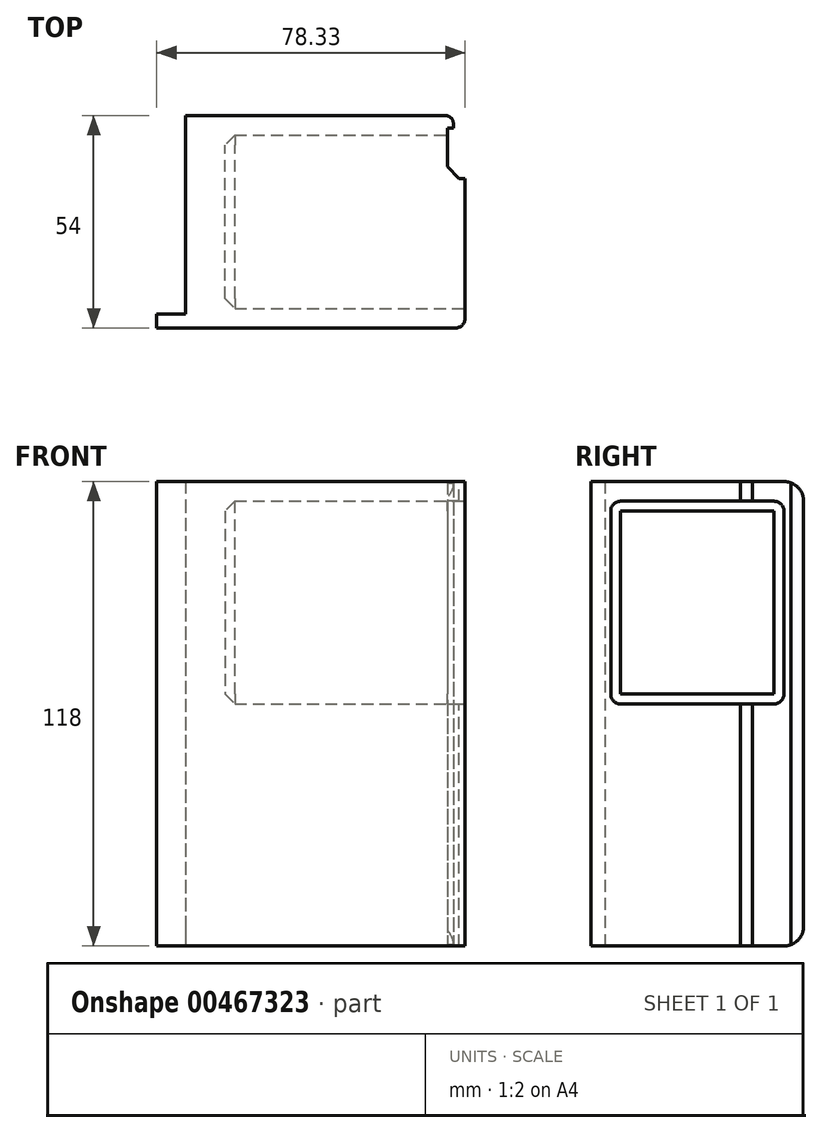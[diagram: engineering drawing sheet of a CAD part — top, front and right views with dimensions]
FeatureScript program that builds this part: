
annotation { "Feature Type Name" : "Feature", "Feature Type Description" : "" }
export const myFeature = defineFeature(function(context is Context, id is Id, definition is map)
    precondition{}
    {
        {
            var Q0;
            Q0=qCreatedBy(makeId("Top.planeOp"),FACE);
            var sketch = newSketch(context, id + "F0", { "sketchPlane" : qUnion([Q0])});
            skLineSegment(sketch, "E0", {"start": v(15.39, 4.66) * mm, "end": v(15.39, 8.16) * mm});
            skLineSegment(sketch, "E1", {"start": v(15.39, 8.16) * mm, "end": v(22.72, 8.16) * mm});
            skLineSegment(sketch, "E2", {"start": v(22.72, 8.16) * mm, "end": v(22.72, 58.66) * mm});
            skLineSegment(sketch, "E3", {"start": v(22.72, 58.66) * mm, "end": v(93.72, 58.66) * mm});
            skLineSegment(sketch, "E4", {"start": v(93.72, 58.66) * mm, "end": v(93.72, 4.66) * mm});
            skLineSegment(sketch, "E5", {"start": v(93.72, 4.66) * mm, "end": v(15.39, 4.66) * mm});
            skLineSegment(sketch, "E6", {"start": v(90.72, 58.66) * mm, "end": v(90.72, 55.46) * mm});
            skLineSegment(sketch, "E7", {"start": v(90.72, 55.46) * mm, "end": v(89.22, 55.46) * mm});
            skLineSegment(sketch, "E8", {"start": v(89.22, 55.46) * mm, "end": v(89.22, 42.66) * mm});
            skLineSegment(sketch, "E9", {"start": v(89.22, 42.66) * mm, "end": v(93.72, 42.66) * mm});
            skSolve(sketch);
        }
        {
            var Q0;
            Q0=makeQuery(id+"F0.imprint","IMPRINT",FACE,{"disambiguationData":[TD([[makeQuery(id+"F0.imprint","IMPRINT",EDGE,{"derivedFrom":sQuery(id+"F0.wireOp",EDGE,"E0")}),-1.0]])]});
            extrude(context, id + "F1", {"entities" : qUnion([Q0]), "depth" : 118 * mm});
        }
        {
            var Q0;
            Q0=makeQuery(id+"F1.opExtrude","SWEPT_FACE",FACE,{"disambiguationData":[OSD([sQuery(id+"F0.wireOp",EDGE,"E4")])]});
            var sketch = newSketch(context, id + "F2", { "sketchPlane" : qUnion([Q0])});
            skLineSegment(sketch, "E10", {"start": v(23.66, 119.82) * mm, "end": v(23.66, 0) * mm, "construction": true});
            skPoint(sketch, "E10.startSnap0", {"position": v(23.66, 118) * mm});
            skLineSegment(sketch, "E11", {"start": v(58.66, 59) * mm, "end": v(4.66, 59) * mm, "construction": true});
            skLineSegment(sketch, "E12", {"start": v(58.66, 78.67) * mm, "end": v(4.66, 78.67) * mm, "construction": true});
            skLineSegment(sketch, "E13.MirrorCS", {"start": v(58.66, 39.33) * mm, "end": v(4.66, 39.33) * mm, "construction": true});
            skLineSegment(sketch, "E14.0", {"start": v(42.66, 118) * mm, "end": v(42.66, 0) * mm});
            skLineSegment(sketch, "E15.0.0", {"start": v(4.66, 0) * mm, "end": v(42.66, 0) * mm});
            skLineSegment(sketch, "E15.0.1", {"start": v(42.66, 0) * mm, "end": v(42.66, 118) * mm});
            skLineSegment(sketch, "E15.0.2", {"start": v(42.66, 118) * mm, "end": v(4.66, 118) * mm});
            skLineSegment(sketch, "E15.0.3", {"start": v(4.66, 118) * mm, "end": v(4.66, 0) * mm});
            skLineSegment(sketch, "E16.bottom", {"start": v(35.16, 113) * mm, "end": v(28.66, 113) * mm});
            skLineSegment(sketch, "E16.top", {"start": v(35.16, 81.17) * mm, "end": v(28.66, 81.17) * mm});
            skLineSegment(sketch, "E16.left", {"start": v(37.66, 110.5) * mm, "end": v(37.66, 83.67) * mm});
            skLineSegment(sketch, "E16.right", {"start": v(26.16, 110.5) * mm, "end": v(26.16, 83.67) * mm});
            skLineSegment(sketch, "E17.MirrorCS", {"start": v(12.16, 113) * mm, "end": v(18.66, 113) * mm});
            skLineSegment(sketch, "E18.MirrorCS", {"start": v(21.16, 110.5) * mm, "end": v(21.16, 83.67) * mm});
            skLineSegment(sketch, "E19.MirrorCS", {"start": v(9.66, 110.5) * mm, "end": v(9.66, 83.67) * mm});
            skLineSegment(sketch, "E20.MirrorCS", {"start": v(12.16, 81.17) * mm, "end": v(18.66, 81.17) * mm});
            skLineSegment(sketch, "E21.MirrorCS", {"start": v(35.16, 76.17) * mm, "end": v(28.66, 76.17) * mm});
            skLineSegment(sketch, "E22.MirrorCS", {"start": v(12.16, 76.17) * mm, "end": v(18.66, 76.17) * mm});
            skLineSegment(sketch, "E23", {"start": v(37.66, 73.67) * mm, "end": v(37.66, 44.33) * mm});
            skLineSegment(sketch, "E24", {"start": v(35.16, 41.83) * mm, "end": v(28.66, 41.83) * mm});
            skLineSegment(sketch, "E25", {"start": v(26.16, 44.33) * mm, "end": v(26.16, 73.67) * mm});
            skLineSegment(sketch, "E26.MirrorCS", {"start": v(21.16, 44.33) * mm, "end": v(21.16, 73.67) * mm});
            skLineSegment(sketch, "E27.MirrorCS", {"start": v(12.16, 41.83) * mm, "end": v(18.66, 41.83) * mm});
            skLineSegment(sketch, "E28.MirrorCS", {"start": v(9.66, 73.67) * mm, "end": v(9.66, 44.33) * mm});
            skLineSegment(sketch, "E29.MirrorCS", {"start": v(35.16, 36.83) * mm, "end": v(28.66, 36.83) * mm});
            skLineSegment(sketch, "E30.MirrorCS", {"start": v(12.16, 36.83) * mm, "end": v(18.66, 36.83) * mm});
            skLineSegment(sketch, "E31", {"start": v(37.66, 34.33) * mm, "end": v(37.66, 7.5) * mm});
            skLineSegment(sketch, "E32", {"start": v(35.16, 5) * mm, "end": v(28.66, 5) * mm});
            skLineSegment(sketch, "E33", {"start": v(26.16, 7.5) * mm, "end": v(26.16, 34.33) * mm});
            skLineSegment(sketch, "E34.MirrorCS", {"start": v(21.16, 7.5) * mm, "end": v(21.16, 34.33) * mm});
            skLineSegment(sketch, "E35.MirrorCS", {"start": v(12.16, 5) * mm, "end": v(18.66, 5) * mm});
            skLineSegment(sketch, "E36.MirrorCS", {"start": v(9.66, 34.33) * mm, "end": v(9.66, 7.5) * mm});
            skPoint(sketch, "E37.visualSharp", {"position": v(37.66, 113) * mm});
            skArc(sketch, "E37.filletArc", {"start": v(37.66, 110.5) * mm, "mid": v(36.92, 112.27) * mm, "end": v(35.16, 113) * mm});
            skPoint(sketch, "E38.visualSharp", {"position": v(26.16, 113) * mm});
            skArc(sketch, "E38.filletArc", {"start": v(28.66, 113) * mm, "mid": v(26.89, 112.27) * mm, "end": v(26.16, 110.5) * mm});
            skPoint(sketch, "E39.visualSharp", {"position": v(26.16, 81.17) * mm});
            skArc(sketch, "E39.filletArc", {"start": v(26.16, 83.67) * mm, "mid": v(26.89, 81.9) * mm, "end": v(28.66, 81.17) * mm});
            skPoint(sketch, "E40.visualSharp", {"position": v(37.66, 81.17) * mm});
            skArc(sketch, "E40.filletArc", {"start": v(35.16, 81.17) * mm, "mid": v(36.92, 81.9) * mm, "end": v(37.66, 83.67) * mm});
            skPoint(sketch, "E41.visualSharp", {"position": v(37.66, 76.17) * mm});
            skArc(sketch, "E41.filletArc", {"start": v(37.66, 73.67) * mm, "mid": v(36.92, 75.43) * mm, "end": v(35.16, 76.17) * mm});
            skPoint(sketch, "E42.visualSharp", {"position": v(26.16, 76.17) * mm});
            skArc(sketch, "E42.filletArc", {"start": v(28.66, 76.17) * mm, "mid": v(26.89, 75.43) * mm, "end": v(26.16, 73.67) * mm});
            skPoint(sketch, "E43.visualSharp", {"position": v(26.16, 41.83) * mm});
            skArc(sketch, "E43.filletArc", {"start": v(26.16, 44.33) * mm, "mid": v(26.89, 42.57) * mm, "end": v(28.66, 41.83) * mm});
            skPoint(sketch, "E44.visualSharp", {"position": v(37.66, 41.83) * mm});
            skArc(sketch, "E44.filletArc", {"start": v(35.16, 41.83) * mm, "mid": v(36.92, 42.57) * mm, "end": v(37.66, 44.33) * mm});
            skPoint(sketch, "E45.visualSharp", {"position": v(37.66, 36.83) * mm});
            skArc(sketch, "E45.filletArc", {"start": v(37.66, 34.33) * mm, "mid": v(36.92, 36.1) * mm, "end": v(35.16, 36.83) * mm});
            skPoint(sketch, "E46.visualSharp", {"position": v(26.16, 36.83) * mm});
            skArc(sketch, "E46.filletArc", {"start": v(28.66, 36.83) * mm, "mid": v(26.89, 36.1) * mm, "end": v(26.16, 34.33) * mm});
            skPoint(sketch, "E47.visualSharp", {"position": v(26.16, 5) * mm});
            skArc(sketch, "E47.filletArc", {"start": v(26.16, 7.5) * mm, "mid": v(26.89, 5.73) * mm, "end": v(28.66, 5) * mm});
            skPoint(sketch, "E48.visualSharp", {"position": v(37.66, 5) * mm});
            skArc(sketch, "E48.filletArc", {"start": v(35.16, 5) * mm, "mid": v(36.92, 5.73) * mm, "end": v(37.66, 7.5) * mm});
            skPoint(sketch, "E49.visualSharp", {"position": v(21.16, 113) * mm});
            skArc(sketch, "E49.filletArc", {"start": v(21.16, 110.5) * mm, "mid": v(20.42, 112.27) * mm, "end": v(18.66, 113) * mm});
            skPoint(sketch, "E50.visualSharp", {"position": v(9.66, 113) * mm});
            skArc(sketch, "E50.filletArc", {"start": v(12.16, 113) * mm, "mid": v(10.39, 112.27) * mm, "end": v(9.66, 110.5) * mm});
            skPoint(sketch, "E51.visualSharp", {"position": v(9.66, 81.17) * mm});
            skArc(sketch, "E51.filletArc", {"start": v(9.66, 83.67) * mm, "mid": v(10.39, 81.9) * mm, "end": v(12.16, 81.17) * mm});
            skPoint(sketch, "E52.visualSharp", {"position": v(21.16, 81.17) * mm});
            skArc(sketch, "E52.filletArc", {"start": v(18.66, 81.17) * mm, "mid": v(20.42, 81.9) * mm, "end": v(21.16, 83.67) * mm});
            skPoint(sketch, "E53.visualSharp", {"position": v(21.16, 76.17) * mm});
            skArc(sketch, "E53.filletArc", {"start": v(21.16, 73.67) * mm, "mid": v(20.42, 75.43) * mm, "end": v(18.66, 76.17) * mm});
            skPoint(sketch, "E54.visualSharp", {"position": v(9.66, 76.17) * mm});
            skArc(sketch, "E54.filletArc", {"start": v(12.16, 76.17) * mm, "mid": v(10.39, 75.43) * mm, "end": v(9.66, 73.67) * mm});
            skPoint(sketch, "E55.visualSharp", {"position": v(21.16, 41.83) * mm});
            skArc(sketch, "E55.filletArc", {"start": v(18.66, 41.83) * mm, "mid": v(20.42, 42.57) * mm, "end": v(21.16, 44.33) * mm});
            skPoint(sketch, "E56.visualSharp", {"position": v(9.66, 41.83) * mm});
            skArc(sketch, "E56.filletArc", {"start": v(9.66, 44.33) * mm, "mid": v(10.39, 42.57) * mm, "end": v(12.16, 41.83) * mm});
            skPoint(sketch, "E57.visualSharp", {"position": v(9.66, 36.83) * mm});
            skArc(sketch, "E57.filletArc", {"start": v(12.16, 36.83) * mm, "mid": v(10.39, 36.1) * mm, "end": v(9.66, 34.33) * mm});
            skPoint(sketch, "E58.visualSharp", {"position": v(21.16, 36.83) * mm});
            skArc(sketch, "E58.filletArc", {"start": v(21.16, 34.33) * mm, "mid": v(20.42, 36.1) * mm, "end": v(18.66, 36.83) * mm});
            skPoint(sketch, "E59.visualSharp", {"position": v(21.16, 5) * mm});
            skArc(sketch, "E59.filletArc", {"start": v(18.66, 5) * mm, "mid": v(20.42, 5.73) * mm, "end": v(21.16, 7.5) * mm});
            skPoint(sketch, "E60.visualSharp", {"position": v(9.66, 5) * mm});
            skArc(sketch, "E60.filletArc", {"start": v(9.66, 7.5) * mm, "mid": v(10.39, 5.73) * mm, "end": v(12.16, 5) * mm});
            skSolve(sketch);
        }
        {
            var Q0;
            Q0=makeQuery(id+"F1.opExtrude","SWEPT_FACE",FACE,{"disambiguationData":[OSD([sQuery(id+"F0.wireOp",EDGE,"E4")])]});
            var sketch = newSketch(context, id + "F3", { "sketchPlane" : qUnion([Q0])});
            skLineSegment(sketch, "E61.0", {"start": v(58.66, 118) * mm, "end": v(58.66, 0) * mm});
            skLineSegment(sketch, "E62.0", {"start": v(4.66, 118) * mm, "end": v(4.66, 0) * mm});
            skLineSegment(sketch, "E63.0", {"start": v(42.66, 118) * mm, "end": v(4.66, 118) * mm});
            skLineSegment(sketch, "E64.0", {"start": v(42.66, 0) * mm, "end": v(4.66, 0) * mm});
            skLineSegment(sketch, "E65.0", {"start": v(55.46, 0) * mm, "end": v(42.66, 0) * mm});
            skLineSegment(sketch, "E66.0", {"start": v(58.66, 0) * mm, "end": v(55.46, 0) * mm});
            skLineSegment(sketch, "E67.0", {"start": v(58.66, 118) * mm, "end": v(55.46, 118) * mm});
            skLineSegment(sketch, "E68.0", {"start": v(55.46, 118) * mm, "end": v(42.66, 118) * mm});
            skLineSegment(sketch, "E69", {"start": v(58.66, 59) * mm, "end": v(4.66, 59) * mm, "construction": true});
            skLineSegment(sketch, "E70.bottom", {"start": v(51.16, 113) * mm, "end": v(12.16, 113) * mm});
            skLineSegment(sketch, "E70.top", {"start": v(51.16, 61.5) * mm, "end": v(12.16, 61.5) * mm});
            skLineSegment(sketch, "E70.left", {"start": v(53.66, 110.5) * mm, "end": v(53.66, 64) * mm});
            skLineSegment(sketch, "E70.right", {"start": v(9.66, 110.5) * mm, "end": v(9.66, 64) * mm});
            skPoint(sketch, "E71.visualSharp", {"position": v(53.66, 113) * mm});
            skArc(sketch, "E71.filletArc", {"start": v(53.66, 110.5) * mm, "mid": v(52.92, 112.27) * mm, "end": v(51.16, 113) * mm});
            skPoint(sketch, "E72.visualSharp", {"position": v(9.66, 113) * mm});
            skArc(sketch, "E72.filletArc", {"start": v(12.16, 113) * mm, "mid": v(10.39, 112.27) * mm, "end": v(9.66, 110.5) * mm});
            skPoint(sketch, "E73.visualSharp", {"position": v(9.66, 61.5) * mm});
            skArc(sketch, "E73.filletArc", {"start": v(9.66, 64) * mm, "mid": v(10.39, 62.23) * mm, "end": v(12.16, 61.5) * mm});
            skPoint(sketch, "E74.visualSharp", {"position": v(53.66, 61.5) * mm});
            skArc(sketch, "E74.filletArc", {"start": v(51.16, 61.5) * mm, "mid": v(52.92, 62.23) * mm, "end": v(53.66, 64) * mm});
            skLineSegment(sketch, "E75.MirrorCS", {"start": v(51.16, 56.5) * mm, "end": v(12.16, 56.5) * mm});
            skArc(sketch, "E76.MirrorCS", {"start": v(9.66, 54) * mm, "mid": v(10.39, 55.77) * mm, "end": v(12.16, 56.5) * mm});
            skLineSegment(sketch, "E77.MirrorCS", {"start": v(9.66, 7.5) * mm, "end": v(9.66, 54) * mm});
            skArc(sketch, "E78.MirrorCS", {"start": v(12.16, 5) * mm, "mid": v(10.39, 5.73) * mm, "end": v(9.66, 7.5) * mm});
            skLineSegment(sketch, "E79.MirrorCS", {"start": v(51.16, 5) * mm, "end": v(12.16, 5) * mm});
            skArc(sketch, "E80.MirrorCS", {"start": v(53.66, 7.5) * mm, "mid": v(52.92, 5.73) * mm, "end": v(51.16, 5) * mm});
            skLineSegment(sketch, "E81.MirrorCS", {"start": v(53.66, 7.5) * mm, "end": v(53.66, 54) * mm});
            skArc(sketch, "E82.MirrorCS", {"start": v(51.16, 56.5) * mm, "mid": v(52.92, 55.77) * mm, "end": v(53.66, 54) * mm});
            skSolve(sketch);
        }
        {
            var Q0;
            Q0=makeQuery(id+"F3.imprint","IMPRINT",FACE,{"disambiguationData":[TD([[makeQuery(id+"F3.imprint","IMPRINT",EDGE,{"derivedFrom":sQuery(id+"F3.wireOp",EDGE,"E70.left")}),-1.0]])]});
            var Q1;
            Q1=makeQuery(id+"F3.imprint","IMPRINT",FACE,{"disambiguationData":[TD([[makeQuery(id+"F3.imprint","IMPRINT",EDGE,{"derivedFrom":sQuery(id+"F3.wireOp",EDGE,"E70.right")}),1.0]])]});
            var Q2;
            {var subQ6=sQuery(id+"F3.wireOp",EDGE,"E76.MirrorCS");Q2=makeQuery(id+"F3.imprint","IMPRINT",FACE,{"disambiguationData":[TD([[makeQuery(id+"F3.imprint","IMPRINT",EDGE,{"derivedFrom":subQ6}),-1.0]])]});}
            var Q3;
            {var subQ0=sQuery(id+"F3.wireOp",EDGE,"E80.MirrorCS");Q3=makeQuery(id+"F3.imprint","IMPRINT",FACE,{"disambiguationData":[TD([[makeQuery(id+"F3.imprint","IMPRINT",EDGE,{"derivedFrom":subQ0}),-1.0]])]});}
            extrude(context, id + "F4", {"entities" : qUnion([Q0, Q1, Q2, Q3]), "operationType" : NewBodyOperationType.REMOVE, "oppositeDirection" : true, "depth" : 61 * mm, "offsetDistance" : 25 * mm});
        }
        {
            var Q0;
            Q0=makeQuery(id+"F4.boolean.opBoolean","COPY",FACE,{"derivedFrom":makeQuery(id+"F4.opExtrude","CAP_FACE",FACE,{"disambiguationData":[OSD([sQuery(id+"F3.wireOp",EDGE,"E70.bottom"),sQuery(id+"F3.wireOp",EDGE,"E70.top"),sQuery(id+"F3.wireOp",EDGE,"E70.left"),sQuery(id+"F3.wireOp",EDGE,"E70.right"),sQuery(id+"F3.wireOp",EDGE,"E71.filletArc"),sQuery(id+"F3.wireOp",EDGE,"E72.filletArc"),sQuery(id+"F3.wireOp",EDGE,"E73.filletArc"),sQuery(id+"F3.wireOp",EDGE,"E74.filletArc")])],"isStart":false})});
            var Q1;
            Q1=makeQuery(id+"F4.boolean.opBoolean","COPY",FACE,{"derivedFrom":makeQuery(id+"F4.opExtrude","CAP_FACE",FACE,{"disambiguationData":[OSD([sQuery(id+"F3.wireOp",EDGE,"E75.MirrorCS"),sQuery(id+"F3.wireOp",EDGE,"E76.MirrorCS"),sQuery(id+"F3.wireOp",EDGE,"E77.MirrorCS"),sQuery(id+"F3.wireOp",EDGE,"E78.MirrorCS"),sQuery(id+"F3.wireOp",EDGE,"E79.MirrorCS"),sQuery(id+"F3.wireOp",EDGE,"E80.MirrorCS"),sQuery(id+"F3.wireOp",EDGE,"E81.MirrorCS"),sQuery(id+"F3.wireOp",EDGE,"E82.MirrorCS")])],"isStart":false})});
            chamfer(context, id + "F5", {"entities" : qUnion([Q0, Q1]), "width" : 2.5 * mm, "tangentPropagation" : true});
        }
        {
            var Q0;
            Q0=makeQuery(id+"F1.opExtrude","CAP_EDGE",EDGE,{"disambiguationData":[OSD([sQuery(id+"F0.wireOp",EDGE,"E3")])],"isStart":false});
            var Q1;
            Q1=makeQuery(id+"F1.opExtrude","CAP_EDGE",EDGE,{"disambiguationData":[OSD([sQuery(id+"F0.wireOp",EDGE,"E3")])],"isStart":true});
            fillet(context, id + "F6", {"entities" : qUnion([Q0, Q1]), "radius" : 5 * mm, "tangentPropagation" : true, "allowEdgeOverflow" : false});
        }
        {
            var Q0;
            Q0=makeQuery(id+"F1.opExtrude","SWEPT_EDGE",EDGE,{"disambiguationData":[OSD([sQuery(id+"F0.wireOp",EDGE,"E8"),sQuery(id+"F0.wireOp",EDGE,"E9")])]});
            chamfer(context, id + "F7", {"entities" : qUnion([Q0]), "width" : 3 * mm, "tangentPropagation" : true});
        }
        {
            var Q0;
            Q0=makeQuery(id+"F1.opExtrude","SWEPT_EDGE",EDGE,{"disambiguationData":[OSD([sQuery(id+"F0.wireOp",EDGE,"E4"),sQuery(id+"F0.wireOp",EDGE,"E5")])]});
            fillet(context, id + "F8", {"entities" : qUnion([Q0]), "radius" : 2.5 * mm, "tangentPropagation" : true, "allowEdgeOverflow" : false});
        }
        {
            var Q0;
            Q0=makeQuery(id+"F1.opExtrude","SWEPT_EDGE",EDGE,{"disambiguationData":[OSD([sQuery(id+"F0.wireOp",EDGE,"E3"),sQuery(id+"F0.wireOp",EDGE,"E6")])]});
            fillet(context, id + "F9", {"entities" : qUnion([Q0]), "radius" : 2 * mm, "allowEdgeOverflow" : false});
        }
    });
